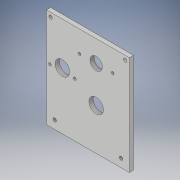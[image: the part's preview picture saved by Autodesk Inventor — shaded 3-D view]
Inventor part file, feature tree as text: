
AUTODESK INVENTOR PART (.ipt)
format: ipt  version: 2018 (Build 220112000, 112)  size: 155,648 bytes
history: native  units: in
note: dims shown in document units (in); Inventor stores cm internally (conversion verified against a paired STEP export)
features: extrude x4, sketch x4
ambient origin geometry x8: Origin, YZ Plane, XZ Plane, XY Plane, X Axis, Y Axis, Z Axis, Center Point
bodies: Solid1 (feature_tree)
feature tree (8):
  extrude  "Extrusion1"  Depth=1.0in
  extrude  "Extrusion2"  Depth=2.2in
  extrude  "Extrusion3"  Depth=0.4466in
  extrude  "Extrusion4"  Depth=0.25in
  sketch  "Sketch1"  dims[d0=0.75in d1=1.0in]
  sketch  "Sketch2"  dims[d2=2.0in d3=2.2in]
  sketch  "Sketch3"  dims[d4=2.25in d5=0.4466in]
  sketch  "Sketch4"  dims[d6=0.875in d7=0.875in d8=2.0in d9=2.0in d10=5.5in d11=1.85in d12=5.0in d13=0.159in d14=0.25in d15=0.25in d16=0.2031in d17=0.25in d18=0.0in d19=5.0in d20=0.5in d21=0.25in d22=0.0in d23=0.5in d24=0.5in d25=0.2031in d26=0.25in d27=0.0in d28=0.75in d29=1.5in d30=0.188in d31=0.159in d32=0.25in d33=0.0in]
